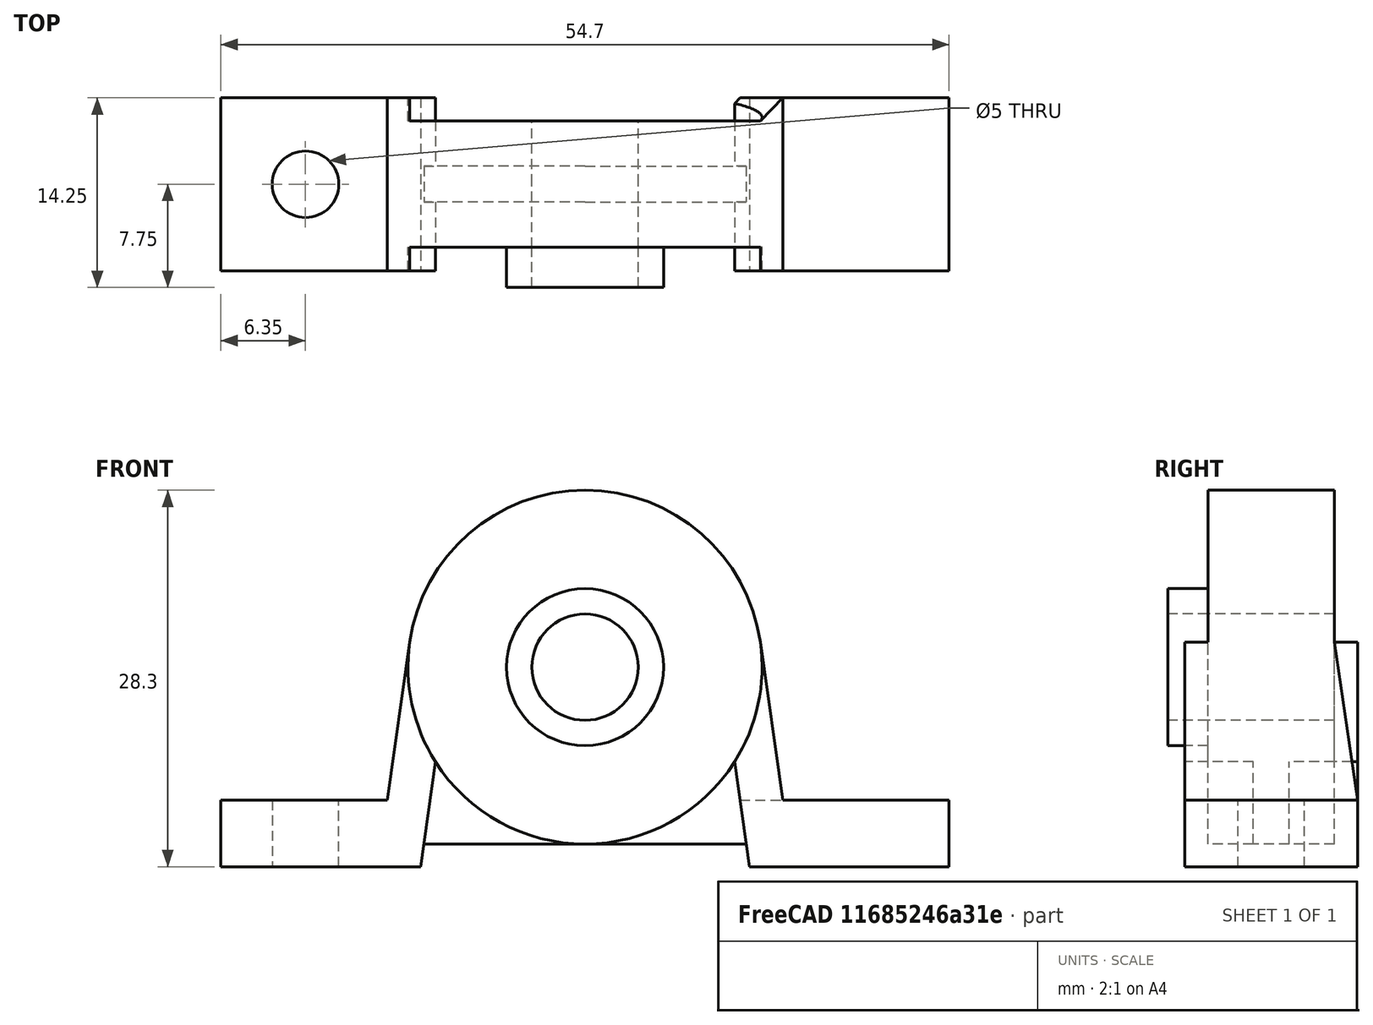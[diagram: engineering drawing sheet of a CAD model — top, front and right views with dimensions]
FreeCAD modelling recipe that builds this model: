
FCSTD DOCUMENT  (FreeCAD 0.20R29410 (Git))
Label: bearing_p08
License: All rights reserved
LicenseURL: http://en.wikipedia.org/wiki/All_rights_reserved
objects: Sketcher::SketchObject×6, PartDesign::Pad×4, PartDesign::CoordinateSystem×3, PartDesign::Mirrored×3, PartDesign::Pocket×2, PartDesign::Body×1, PartDesign::MultiTransform×1
note: 26 computed .brp shape members not serialized (recipe doc carries the construction recipe); baked Part::Feature solids carry a one-line shape summary decoded from their .brp

FEATURE [PartDesign::CoordinateSystem] LCS_0  label="base"
  AttacherType = Attacher::AttachEngine3D
  MapMode = 2
  Support = -> [X_Axis]
FEATURE [Sketcher::SketchObject] Sketch
  FullyConstrained = true
  MapMode = 5
  Placement = pos=(0,0,0) rot=(1,0,0;1.5708rad)
  Support = -> [XZ_Plane]
  sketch-geometry (11):
    g0: LineSegment StartX=12.35 StartY=0 StartZ=0 EndX=27.35 EndY=0 EndZ=0
    g1: LineSegment StartX=27.35 StartY=0 StartZ=0 EndX=27.35 EndY=5 EndZ=0
    g2: LineSegment StartX=27.35 StartY=5 StartZ=0 EndX=14.85 EndY=5 EndZ=0
    g3: LineSegment StartX=14.85 StartY=5 StartZ=0 EndX=13.1684 EndY=16.8661 EndZ=0
    g4: LineSegment StartX=12.35 StartY=0 StartZ=0 EndX=11.2334 EndY=7.87952 EndZ=0
    g5: ArcOfCircle CenterX=0 CenterY=15 CenterZ=0 NormalX=0 NormalY=0 NormalZ=1 AngleXU=0 Radius=4 StartAngle=4.71239 EndAngle=7.85398
    g6: ArcOfCircle CenterX=0 CenterY=15 CenterZ=0 NormalX=0 NormalY=0 NormalZ=1 AngleXU=0 Radius=13.3 StartAngle=4.71239 EndAngle=5.71823
    g7: ArcOfCircle CenterX=0 CenterY=15 CenterZ=0 NormalX=0 NormalY=0 NormalZ=1 AngleXU=0 Radius=13.3 StartAngle=0.140774 EndAngle=1.5708
    g8: LineSegment StartX=1.2e-15 StartY=19 StartZ=0 EndX=8e-16 EndY=28.3 EndZ=0
    g9: LineSegment StartX=-2.4e-15 StartY=1.7 StartZ=0 EndX=-7e-16 EndY=11 EndZ=0
    g10: ArcOfCircle CenterX=0 CenterY=15 CenterZ=0 NormalX=0 NormalY=0 NormalZ=1 AngleXU=0 Radius=13.3 StartAngle=5.71823 EndAngle=6.42396
  constraints (33):
    c: PointOnObject(g0,g-1)
    c: PointOnObject(g0,g-1)
    c: Coincident(g0,g1)
    c: Vertical(g1)
    c: Coincident(g1,g2)
    c: Horizontal(g2)
    c: Coincident(g2,g3)
    c: Coincident(g0,g4)
    c: PointOnObject(g5,g-2)
    c: PointOnObject(g5,g-2)
    c: PointOnObject(g5,g-2)
    c: Coincident(g6,g5)
    c: Coincident(g6,g4)
    c: Coincident(g7,g5)
    c: PointOnObject(g7,g-2)
    c: PointOnObject(g6,g-2)
    c: Diameter(g5) = 8
    c: Distance(g1) = 5
    c: DistanceX(g0) = 27.35
    c: Coincident(g8,g5)
    c: Coincident(g8,g7)
    c: Coincident(g9,g6)
    c: Coincident(g9,g5)
    c: Distance(g0) = 15
    c: Distance(g2) = 12.5
    c: DistanceY(g7) = 28.3
    c: DistanceY(g6,g7) = 26.6
    c: Parallel(g4,g3)
    c: Tangent(g7,g3) = -1.5708
    c: Coincident(g10,g5)
    c: Coincident(g10,g4)
    c: Coincident(g10,g3)
    c: DistanceY(g10) = 15
FEATURE [PartDesign::Pad] Pad
  Direction = (0,-1,-2e-16)
  Length = 13
  Length2 = 10
  Midplane = true
  Placement = pos=(0,0,0) rot=(1,0,0;1.5708rad)
  Profile = -> Sketch
  ReferenceAxis = -> Sketch [N_Axis]
  Type = 0
FEATURE [Sketcher::SketchObject] Sketch001
  AttachmentOffset = pos=(0,0,7) rot=(0,0,1;0rad)
  FullyConstrained = true
  MapMode = 5
  Placement = pos=(7,-1.6e-15,1.6e-15) rot=(0.57735,0.57735,0.57735;2.0944rad)
  Support = -> [YZ_Plane]
  expr: Constraints[16] = Sketch.Constraints[16]
  expr: Constraints[17] = Sketch.Constraints[17]
  expr: Constraints[18] = Sketch.Constraints[18]
  expr: Constraints[23] = Sketch.Constraints[23]
  expr: Constraints[24] = Sketch.Constraints[24]
  expr: Constraints[25] = Sketch.Constraints[25]
  expr: Constraints[26] = Sketch.Constraints[26]
  expr: Constraints[39] = Pad.Length / 2
  sketch-geometry (14):
    g0: LineSegment StartX=12.35 StartY=0 StartZ=0 EndX=27.35 EndY=0 EndZ=0
    g1: LineSegment StartX=27.35 StartY=0 StartZ=0 EndX=27.35 EndY=5 EndZ=0
    g2: LineSegment StartX=27.35 StartY=5 StartZ=0 EndX=14.85 EndY=5 EndZ=0
    g3: LineSegment StartX=14.85 StartY=5 StartZ=0 EndX=13.1684 EndY=16.8661 EndZ=0
    g4: LineSegment StartX=12.35 StartY=0 StartZ=0 EndX=11.2334 EndY=7.87952 EndZ=0
    g5: ArcOfCircle CenterX=0 CenterY=15 CenterZ=0 NormalX=0 NormalY=0 NormalZ=1 AngleXU=0 Radius=4 StartAngle=4.71239 EndAngle=7.85398
    g6: ArcOfCircle CenterX=0 CenterY=15 CenterZ=0 NormalX=0 NormalY=0 NormalZ=1 AngleXU=0 Radius=13.3 StartAngle=4.71239 EndAngle=5.71823
    g7: ArcOfCircle CenterX=0 CenterY=15 CenterZ=0 NormalX=0 NormalY=0 NormalZ=1 AngleXU=0 Radius=13.3 StartAngle=0.140774 EndAngle=1.5708
    g8: LineSegment StartX=1.2e-15 StartY=19 StartZ=0 EndX=8e-16 EndY=28.3 EndZ=0
    g9: LineSegment StartX=-2.4e-15 StartY=1.7 StartZ=0 EndX=-7e-16 EndY=11 EndZ=0
    g10: ArcOfCircle CenterX=0 CenterY=15 CenterZ=0 NormalX=0 NormalY=0 NormalZ=1 AngleXU=0 Radius=13.3 StartAngle=5.71823 EndAngle=6.42396
    g11: LineSegment StartX=6.5 StartY=5 StartZ=0 EndX=4.75 EndY=16.8661 EndZ=0
    g12: LineSegment StartX=4.75 StartY=16.8661 StartZ=0 EndX=6.5 EndY=16.8661 EndZ=0
    g13: LineSegment StartX=6.5 StartY=16.8661 StartZ=0 EndX=6.5 EndY=5 EndZ=0
  constraints (41):
    c: PointOnObject(g0,g-1)
    c: PointOnObject(g0,g-1)
    c: Coincident(g0,g1)
    c: Vertical(g1)
    c: Coincident(g1,g2)
    c: Horizontal(g2)
    c: Coincident(g2,g3)
    c: Coincident(g0,g4)
    c: PointOnObject(g5,g-2)
    c: PointOnObject(g5,g-2)
    c: PointOnObject(g5,g-2)
    c: Coincident(g6,g5)
    c: Coincident(g6,g4)
    c: Coincident(g7,g5)
    c: PointOnObject(g7,g-2)
    c: PointOnObject(g6,g-2)
    c: Diameter(g5) = 8
    c: Distance(g1) = 5
    c: DistanceX(g0) = 27.35
    c: Coincident(g8,g5)
    c: Coincident(g8,g7)
    c: Coincident(g9,g6)
    c: Coincident(g9,g5)
    c: Distance(g0) = 15
    c: Distance(g2) = 12.5
    c: DistanceY(g7) = 28.3
    c: DistanceY(g6,g7) = 26.6
    c: Parallel(g4,g3)
    c: Tangent(g7,g3) = -1.5708
    c: Coincident(g10,g5)
    c: Coincident(g10,g4)
    c: Coincident(g10,g3)
    c: Coincident(g12,g11)
    c: Horizontal(g12)
    c: Coincident(g13,g12)
    c: Coincident(g13,g11)
    c: Vertical(g13)
    c: Horizontal(g1,g11)
    c: Horizontal(g12,g3)
    c: DistanceX(g11) = 6.5
    c: DistanceX(g11) = 4.75
FEATURE [PartDesign::Pocket] Pocket
  BaseFeature = -> Pad
  Direction = (-1,2e-16,-3e-16)
  Length = 5
  Length2 = 5
  Placement = pos=(0,0,0) rot=(1,0,0;1.5708rad)
  Profile = -> Sketch001
  ReferenceAxis = -> Sketch001 [N_Axis]
  Reversed = true
  Type = 1
FEATURE [Sketcher::SketchObject] Sketch002
  FullyConstrained = true
  MapMode = 5
  Placement = pos=(0,0,0) rot=(1,0,0;1.5708rad)
  Support = -> [XZ_Plane]
  expr: Constraints[16] = Sketch.Constraints[16]
  expr: Constraints[17] = Sketch.Constraints[17]
  expr: Constraints[18] = Sketch.Constraints[18]
  expr: Constraints[23] = Sketch.Constraints[23]
  expr: Constraints[24] = Sketch.Constraints[24]
  expr: Constraints[25] = Sketch.Constraints[25]
  expr: Constraints[26] = Sketch.Constraints[26]
  expr: Constraints[48] = Sketch.Constraints[16]
  expr: Constraints[49] = Sketch.Constraints[17]
  expr: Constraints[50] = Sketch.Constraints[18]
  expr: Constraints[55] = Sketch.Constraints[23]
  expr: Constraints[56] = Sketch.Constraints[24]
  expr: Constraints[57] = Sketch.Constraints[25]
  expr: Constraints[58] = Sketch.Constraints[26]
  sketch-geometry (22):
    g0: LineSegment StartX=12.35 StartY=0 StartZ=0 EndX=27.35 EndY=0 EndZ=0
    g1: LineSegment StartX=27.35 StartY=0 StartZ=0 EndX=27.35 EndY=5 EndZ=0
    g2: LineSegment StartX=27.35 StartY=5 StartZ=0 EndX=14.85 EndY=5 EndZ=0
    g3: LineSegment StartX=14.85 StartY=5 StartZ=0 EndX=13.1684 EndY=16.8661 EndZ=0
    g4: LineSegment StartX=12.35 StartY=0 StartZ=0 EndX=11.2334 EndY=7.87952 EndZ=0
    g5: ArcOfCircle CenterX=0 CenterY=15 CenterZ=0 NormalX=0 NormalY=0 NormalZ=1 AngleXU=0 Radius=4 StartAngle=4.71239 EndAngle=7.85398
    g6: ArcOfCircle CenterX=0 CenterY=15 CenterZ=0 NormalX=0 NormalY=0 NormalZ=1 AngleXU=0 Radius=13.3 StartAngle=4.71239 EndAngle=5.71823
    g7: ArcOfCircle CenterX=0 CenterY=15 CenterZ=0 NormalX=0 NormalY=0 NormalZ=1 AngleXU=0 Radius=13.3 StartAngle=0.140774 EndAngle=1.5708
    g8: LineSegment StartX=1.2e-15 StartY=19 StartZ=0 EndX=8e-16 EndY=28.3 EndZ=0
    g9: LineSegment StartX=-2.4e-15 StartY=1.7 StartZ=0 EndX=-7e-16 EndY=11 EndZ=0
    g10: ArcOfCircle CenterX=0 CenterY=15 CenterZ=0 NormalX=0 NormalY=0 NormalZ=1 AngleXU=0 Radius=13.3 StartAngle=5.71823 EndAngle=6.42396
    g11: LineSegment StartX=12.35 StartY=0 StartZ=0 EndX=27.35 EndY=0 EndZ=0
    g12: LineSegment StartX=27.35 StartY=0 StartZ=0 EndX=27.35 EndY=5 EndZ=0
    g13: LineSegment StartX=27.35 StartY=5 StartZ=0 EndX=14.85 EndY=5 EndZ=0
    g14: LineSegment StartX=14.85 StartY=5 StartZ=0 EndX=13.1684 EndY=16.8661 EndZ=0
    g15: LineSegment StartX=12.35 StartY=0 StartZ=0 EndX=11.2334 EndY=7.87952 EndZ=0
    g16: ArcOfCircle CenterX=0 CenterY=15 CenterZ=0 NormalX=0 NormalY=0 NormalZ=1 AngleXU=0 Radius=4 StartAngle=4.71239 EndAngle=7.85398
    g17: ArcOfCircle CenterX=0 CenterY=15 CenterZ=0 NormalX=0 NormalY=0 NormalZ=1 AngleXU=0 Radius=13.3 StartAngle=4.71239 EndAngle=5.71823
    g18: ArcOfCircle CenterX=0 CenterY=15 CenterZ=0 NormalX=0 NormalY=0 NormalZ=1 AngleXU=0 Radius=13.3 StartAngle=0.140774 EndAngle=1.5708
    g19: LineSegment StartX=1.2e-15 StartY=19 StartZ=0 EndX=8e-16 EndY=28.3 EndZ=0
    g20: LineSegment StartX=-2.4e-15 StartY=1.7 StartZ=0 EndX=-7e-16 EndY=11 EndZ=0
    g21: ArcOfCircle CenterX=0 CenterY=15 CenterZ=0 NormalX=0 NormalY=0 NormalZ=1 AngleXU=0 Radius=13.3 StartAngle=5.71823 EndAngle=6.42396
  constraints (64):
    c: PointOnObject(g0,g-1)
    c: PointOnObject(g0,g-1)
    c: Coincident(g0,g1)
    c: Vertical(g1)
    c: Coincident(g1,g2)
    c: Horizontal(g2)
    c: Coincident(g2,g3)
    c: Coincident(g0,g4)
    c: PointOnObject(g5,g-2)
    c: PointOnObject(g5,g-2)
    c: PointOnObject(g5,g-2)
    c: Coincident(g6,g5)
    c: Coincident(g6,g4)
    c: Coincident(g7,g5)
    c: PointOnObject(g7,g-2)
    c: PointOnObject(g6,g-2)
    c: Diameter(g5) = 8
    c: Distance(g1) = 5
    c: DistanceX(g0) = 27.35
    c: Coincident(g8,g5)
    c: Coincident(g8,g7)
    c: Coincident(g9,g6)
    c: Coincident(g9,g5)
    c: Distance(g0) = 15
    c: Distance(g2) = 12.5
    c: DistanceY(g7) = 28.3
    c: DistanceY(g6,g7) = 26.6
    c: Parallel(g4,g3)
    c: Tangent(g7,g3) = -1.5708
    c: Coincident(g10,g5)
    c: Coincident(g10,g4)
    c: Coincident(g10,g3)
    c: PointOnObject(g11,g-1)
    c: PointOnObject(g11,g-1)
    c: Coincident(g11,g12)
    c: Vertical(g12)
    c: Coincident(g12,g13)
    c: Horizontal(g13)
    c: Coincident(g13,g14)
    c: Coincident(g11,g15)
    c: PointOnObject(g16,g-2)
    c: PointOnObject(g16,g-2)
    c: PointOnObject(g16,g-2)
    c: Coincident(g17,g16)
    c: Coincident(g17,g15)
    c: Coincident(g18,g16)
    c: PointOnObject(g18,g-2)
    c: PointOnObject(g17,g-2)
    c: Diameter(g16) = 8
    c: Distance(g12) = 5
    c: DistanceX(g11) = 27.35
    c: Coincident(g19,g16)
    c: Coincident(g19,g18)
    c: Coincident(g20,g17)
    c: Coincident(g20,g16)
    c: Distance(g11) = 15
    c: Distance(g13) = 12.5
    c: DistanceY(g18) = 28.3
    c: DistanceY(g17,g18) = 26.6
    c: Parallel(g15,g14)
    c: Tangent(g18,g14) = -1.5708
    c: Coincident(g21,g16)
    c: Coincident(g21,g15)
    c: Coincident(g21,g14)
FEATURE [PartDesign::Pad] Pad001
  BaseFeature = -> Pocket
  Direction = (0,-1,-2e-16)
  Length = 9.5
  Length2 = 10
  Midplane = true
  Placement = pos=(0,0,0) rot=(1,0,0;1.5708rad)
  Profile = -> Sketch002
  ReferenceAxis = -> Sketch002 [N_Axis]
  Type = 0
FEATURE [Sketcher::SketchObject] Sketch003
  FullyConstrained = false
  MapMode = 5
  Placement = pos=(0,0,0) rot=(1,0,0;1.5708rad)
  Support = -> [XZ_Plane]
  expr: Constraints[16] = Sketch002.Constraints[16]
  expr: Constraints[17] = Sketch002.Constraints[17]
  expr: Constraints[18] = Sketch002.Constraints[18]
  expr: Constraints[23] = Sketch002.Constraints[23]
  expr: Constraints[24] = Sketch002.Constraints[24]
  expr: Constraints[25] = Sketch002.Constraints[25]
  expr: Constraints[26] = Sketch002.Constraints[26]
  expr: Constraints[45] = Sketch002.Constraints[48]
  expr: Constraints[46] = Sketch002.Constraints[49]
  expr: Constraints[47] = Sketch002.Constraints[50]
  expr: Constraints[52] = Sketch002.Constraints[55]
  expr: Constraints[53] = Sketch002.Constraints[56]
  expr: Constraints[54] = Sketch002.Constraints[57]
  expr: Constraints[55] = Sketch002.Constraints[58]
  sketch-geometry (23):
    g0: LineSegment StartX=12.35 StartY=0 StartZ=0 EndX=27.35 EndY=0 EndZ=0
    g1: LineSegment StartX=27.35 StartY=0 StartZ=0 EndX=27.35 EndY=5 EndZ=0
    g2: LineSegment StartX=27.35 StartY=5 StartZ=0 EndX=14.85 EndY=5 EndZ=0
    g3: LineSegment StartX=14.85 StartY=5 StartZ=0 EndX=13.1684 EndY=16.8661 EndZ=0
    g4: ArcOfCircle CenterX=0 CenterY=15 CenterZ=0 NormalX=0 NormalY=0 NormalZ=1 AngleXU=0 Radius=4 StartAngle=4.71239 EndAngle=7.85398
    g5: ArcOfCircle CenterX=0 CenterY=15 CenterZ=0 NormalX=0 NormalY=0 NormalZ=1 AngleXU=0 Radius=13.3 StartAngle=4.71239 EndAngle=5.71823
    g6: ArcOfCircle CenterX=0 CenterY=15 CenterZ=0 NormalX=0 NormalY=0 NormalZ=1 AngleXU=0 Radius=13.3 StartAngle=0.140774 EndAngle=1.5708
    g7: LineSegment StartX=0 StartY=19 StartZ=0 EndX=8e-16 EndY=28.3 EndZ=0
    g8: LineSegment StartX=-2.4e-15 StartY=1.7 StartZ=0 EndX=-7e-16 EndY=11 EndZ=0
    g9: ArcOfCircle CenterX=0 CenterY=15 CenterZ=0 NormalX=0 NormalY=0 NormalZ=1 AngleXU=0 Radius=13.3 StartAngle=5.71823 EndAngle=6.42396
    g10: LineSegment StartX=12.35 StartY=0 StartZ=0 EndX=27.35 EndY=0 EndZ=0
    g11: LineSegment StartX=27.35 StartY=0 StartZ=0 EndX=27.35 EndY=5 EndZ=0
    g12: LineSegment StartX=27.35 StartY=5 StartZ=0 EndX=14.85 EndY=5 EndZ=0
    g13: LineSegment StartX=14.85 StartY=5 StartZ=0 EndX=13.1684 EndY=16.8661 EndZ=0
    g14: ArcOfCircle CenterX=0 CenterY=15 CenterZ=0 NormalX=0 NormalY=0 NormalZ=1 AngleXU=0 Radius=4 StartAngle=4.71239 EndAngle=7.85398
    g15: ArcOfCircle CenterX=0 CenterY=15 CenterZ=0 NormalX=0 NormalY=0 NormalZ=1 AngleXU=0 Radius=13.3 StartAngle=4.71239 EndAngle=5.71823
    g16: ArcOfCircle CenterX=0 CenterY=15 CenterZ=0 NormalX=0 NormalY=0 NormalZ=1 AngleXU=0 Radius=13.3 StartAngle=0.140774 EndAngle=1.5708
    g17: LineSegment StartX=1.2e-15 StartY=19 StartZ=0 EndX=8e-16 EndY=28.3 EndZ=0
    g18: LineSegment StartX=-2.4e-15 StartY=1.7 StartZ=0 EndX=-7e-16 EndY=11 EndZ=0
    g19: ArcOfCircle CenterX=0 CenterY=15 CenterZ=0 NormalX=0 NormalY=0 NormalZ=1 AngleXU=0 Radius=13.3 StartAngle=5.71823 EndAngle=6.42396
    g20: LineSegment StartX=-2.4e-15 StartY=1.7 StartZ=0 EndX=12.1091 EndY=1.7 EndZ=0
    g21: LineSegment StartX=12.35 StartY=0 StartZ=0 EndX=12.1091 EndY=1.7 EndZ=0
    g22: LineSegment StartX=12.1091 StartY=1.7 StartZ=0 EndX=11.2334 EndY=7.87952 EndZ=0
  constraints (65):
    c: PointOnObject(g0,g-1)
    c: PointOnObject(g0,g-1)
    c: Coincident(g0,g1)
    c: Vertical(g1)
    c: Coincident(g1,g2)
    c: Horizontal(g2)
    c: Coincident(g2,g3)
    c: Coincident(g0,g21)
    c: PointOnObject(g4,g-2)
    c: PointOnObject(g4,g-2)
    c: PointOnObject(g4,g-2)
    c: Coincident(g5,g4)
    c: Coincident(g5,g22)
    c: Coincident(g6,g4)
    c: PointOnObject(g6,g-2)
    c: PointOnObject(g5,g-2)
    c: Diameter(g4) = 8
    c: Distance(g1) = 5
    c: DistanceX(g0) = 27.35
    c: Coincident(g7,g4)
    c: Coincident(g7,g6)
    c: Coincident(g8,g5)
    c: Coincident(g8,g4)
    c: Distance(g0) = 15
    c: Distance(g2) = 12.5
    c: DistanceY(g6) = 28.3
    c: DistanceY(g5,g6) = 26.6
    c: Tangent(g6,g3) = -1.5708
    c: Coincident(g9,g4)
    c: Coincident(g9,g22)
    c: Coincident(g9,g3)
    c: PointOnObject(g10,g-1)
    c: PointOnObject(g10,g-1)
    c: Coincident(g10,g11)
    c: Vertical(g11)
    c: Coincident(g11,g12)
    c: Horizontal(g12)
    c: Coincident(g12,g13)
    c: PointOnObject(g14,g-2)
    c: PointOnObject(g14,g-2)
    c: PointOnObject(g14,g-2)
    c: Coincident(g15,g14)
    c: Coincident(g16,g14)
    c: PointOnObject(g16,g-2)
    c: PointOnObject(g15,g-2)
    c: Diameter(g14) = 8
    c: Distance(g11) = 5
    c: DistanceX(g10) = 27.35
    c: Coincident(g17,g14)
    c: Coincident(g17,g16)
    c: Coincident(g18,g15)
    c: Coincident(g18,g14)
    c: Distance(g10) = 15
    c: Distance(g12) = 12.5
    c: DistanceY(g16) = 28.3
    c: DistanceY(g15,g16) = 26.6
    c: Tangent(g16,g13) = -1.5708
    c: Coincident(g19,g14)
    c: Coincident(g19,g13)
    c: Coincident(g20,g5)
    c: Horizontal(g20)
    c: Coincident(g21,g22)
    c: Parallel(g21,g3)
    c: Parallel(g22,g3)
    c: Coincident(g21,g20)
FEATURE [PartDesign::Pad] Pad002
  BaseFeature = -> Pad001
  Direction = (0,-1,-2e-16)
  Length = 2.7
  Length2 = 10
  Midplane = true
  Placement = pos=(0,0,0) rot=(1,0,0;1.5708rad)
  Profile = -> Sketch003
  ReferenceAxis = -> Sketch003 [N_Axis]
  Type = 0
FEATURE [Sketcher::SketchObject] Sketch004
  FullyConstrained = true
  MapMode = 5
  Placement = pos=(0,0,0) rot=(1,0,0;1.5708rad)
  Support = -> [XZ_Plane]
  expr: Constraints[16] = Sketch.Constraints[16]
  expr: Constraints[17] = Sketch.Constraints[17]
  expr: Constraints[18] = Sketch.Constraints[18]
  expr: Constraints[23] = Sketch.Constraints[23]
  expr: Constraints[24] = Sketch.Constraints[24]
  expr: Constraints[25] = Sketch.Constraints[25]
  expr: Constraints[26] = Sketch.Constraints[26]
  sketch-geometry (14):
    g0: LineSegment StartX=12.35 StartY=0 StartZ=0 EndX=27.35 EndY=0 EndZ=0
    g1: LineSegment StartX=27.35 StartY=0 StartZ=0 EndX=27.35 EndY=5 EndZ=0
    g2: LineSegment StartX=27.35 StartY=5 StartZ=0 EndX=14.85 EndY=5 EndZ=0
    g3: LineSegment StartX=14.85 StartY=5 StartZ=0 EndX=13.1684 EndY=16.8661 EndZ=0
    g4: LineSegment StartX=12.35 StartY=0 StartZ=0 EndX=11.2334 EndY=7.87952 EndZ=0
    g5: ArcOfCircle CenterX=0 CenterY=15 CenterZ=0 NormalX=0 NormalY=0 NormalZ=1 AngleXU=0 Radius=4 StartAngle=4.71239 EndAngle=7.85398
    g6: ArcOfCircle CenterX=0 CenterY=15 CenterZ=0 NormalX=0 NormalY=0 NormalZ=1 AngleXU=0 Radius=13.3 StartAngle=4.71239 EndAngle=5.71823
    g7: ArcOfCircle CenterX=0 CenterY=15 CenterZ=0 NormalX=0 NormalY=0 NormalZ=1 AngleXU=0 Radius=13.3 StartAngle=0.140774 EndAngle=1.5708
    g8: ArcOfCircle CenterX=0 CenterY=15 CenterZ=0 NormalX=0 NormalY=0 NormalZ=1 AngleXU=0 Radius=13.3 StartAngle=5.71823 EndAngle=6.42396
    g9: ArcOfCircle CenterX=0 CenterY=15 CenterZ=0 NormalX=0 NormalY=0 NormalZ=1 AngleXU=0 Radius=5.9 StartAngle=4.71239 EndAngle=7.85398
    g10: LineSegment StartX=1.2e-15 StartY=19 StartZ=0 EndX=8e-16 EndY=20.9 EndZ=0
    g11: LineSegment StartX=8e-16 StartY=20.9 StartZ=0 EndX=8e-16 EndY=28.3 EndZ=0
    g12: LineSegment StartX=-1.1e-15 StartY=1.7 StartZ=0 EndX=-1.1e-15 EndY=9.1 EndZ=0
    g13: LineSegment StartX=-1.1e-15 StartY=9.1 StartZ=0 EndX=-7e-16 EndY=11 EndZ=0
  constraints (40):
    c: PointOnObject(g0,g-1)
    c: PointOnObject(g0,g-1)
    c: Coincident(g0,g1)
    c: Vertical(g1)
    c: Coincident(g1,g2)
    c: Horizontal(g2)
    c: Coincident(g2,g3)
    c: Coincident(g0,g4)
    c: PointOnObject(g5,g-2)
    c: PointOnObject(g5,g-2)
    c: PointOnObject(g5,g-2)
    c: Coincident(g6,g5)
    c: Coincident(g6,g4)
    c: Coincident(g7,g5)
    c: PointOnObject(g7,g-2)
    c: PointOnObject(g6,g-2)
    c: Diameter(g5) = 8
    c: Distance(g1) = 5
    c: DistanceX(g0) = 27.35
    c: Coincident(g10,g5)
    c: Coincident(g11,g7)
    c: Coincident(g12,g6)
    c: Coincident(g13,g5)
    c: Distance(g0) = 15
    c: Distance(g2) = 12.5
    c: DistanceY(g7) = 28.3
    c: DistanceY(g6,g7) = 26.6
    c: Parallel(g4,g3)
    c: Tangent(g7,g3) = -1.5708
    c: Coincident(g8,g5)
    c: Coincident(g8,g4)
    c: Coincident(g8,g3)
    c: Coincident(g9,g5)
    c: Diameter(g9) = 11.8
    c: Coincident(g10,g11)
    c: Coincident(g12,g13)
    c: Coincident(g12,g9)
    c: Coincident(g10,g9)
    c: Vertical(g11)
    c: Vertical(g12)
FEATURE [PartDesign::Pad] Pad003
  BaseFeature = -> Pad002
  Direction = (0,-1,-2e-16)
  Length = 7.75
  Length2 = 10
  Placement = pos=(0,0,0) rot=(1,0,0;1.5708rad)
  Profile = -> Sketch004
  ReferenceAxis = -> Sketch004 [N_Axis]
  Type = 0
FEATURE [PartDesign::Mirrored] Mirrored001
  MirrorPlane = -> Sketch001 [V_Axis]
  Placement = pos=(0,0,0) rot=(1,0,0;1.5708rad)
FEATURE [PartDesign::Mirrored] Mirrored002
  MirrorPlane = -> YZ_Plane
  Placement = pos=(0,0,0) rot=(1,0,0;1.5708rad)
FEATURE [Sketcher::SketchObject] Sketch005
  FullyConstrained = true
  MapMode = 5
  Support = -> [XY_Plane]
  sketch-geometry (1):
    g0: Circle CenterX=21 CenterY=0 CenterZ=0 NormalX=0 NormalY=0 NormalZ=1 AngleXU=0 Radius=2.5
  constraints (3):
    c: PointOnObject(g0,g-1)
    c: Diameter(g0) = 5
    c: DistanceX(g0) = 21
FEATURE [PartDesign::Body] p08
  Group = -> [LCS_0,Sketch,Pad,Sketch001,Pocket,Sketch002,Pad001,Sketch003,Pad002,Sketch004,Pad003,Mirrored,Local_CS,Local_CS001,MultiTransform,Mirrored001,Mirrored002,Sketch005,Pocket001]
  Origin = -> Origin
  Tip = -> Mirrored
FEATURE [PartDesign::Mirrored] Mirrored
  BaseFeature = -> Pad003
  MirrorPlane = -> Sketch [V_Axis]
  Originals = -> [Pad,Pad001,Pad002,Pad003,Pocket001]
  Placement = pos=(0,0,0) rot=(1,0,0;1.5708rad)
FEATURE [PartDesign::MultiTransform] MultiTransform
  BaseFeature = -> Mirrored
  Originals = -> [Pocket]
  Placement = pos=(0,0,0) rot=(1,0,0;1.5708rad)
  Transformations = -> [Mirrored001,Mirrored002]
FEATURE [PartDesign::Pocket] Pocket001
  BaseFeature = -> MultiTransform
  Direction = (0,0,-1)
  Length = 5
  Length2 = 5
  Midplane = true
  Placement = pos=(0,0,0) rot=(1,0,0;1.5708rad)
  Profile = -> Sketch005
  ReferenceAxis = -> Sketch005 [N_Axis]
  Type = 1
FEATURE [PartDesign::CoordinateSystem] Local_CS  label="back"
  AttacherType = Attacher::AttachEngine3D
  MapMode = 11
  Placement = pos=(0,4.75,15) rot=(0,0.707107,0.707107;3.14159rad)
  Support = -> [Pocket001]
FEATURE [PartDesign::CoordinateSystem] Local_CS001  label="front"
  AttacherType = Attacher::AttachEngine3D
  MapMode = 11
  Placement = pos=(0,-7.75,15) rot=(1,0,0;1.5708rad)
  Support = -> [Pocket001]
